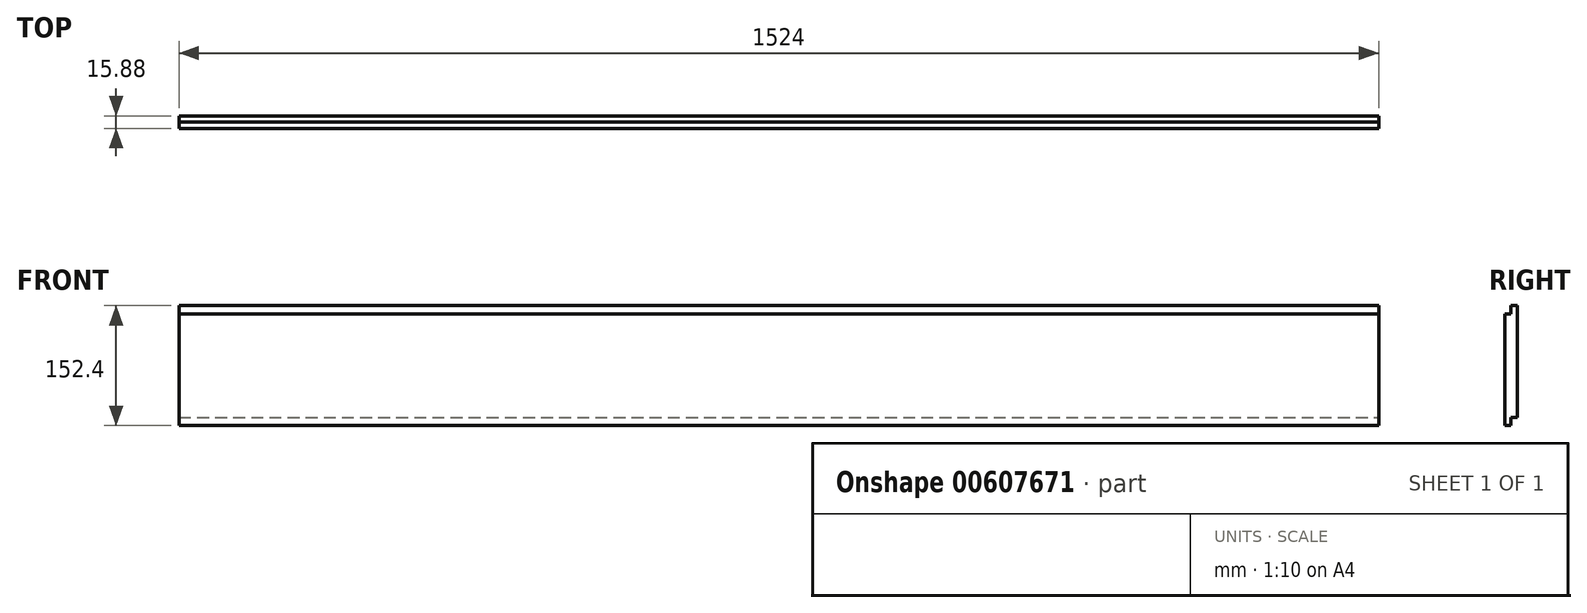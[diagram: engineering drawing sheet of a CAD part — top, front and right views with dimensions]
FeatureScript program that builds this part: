
annotation { "Feature Type Name" : "Feature", "Feature Type Description" : "" }
export const myFeature = defineFeature(function(context is Context, id is Id, definition is map)
    precondition{}
    {
        {
            var Q0;
            Q0=qCreatedBy(makeId("Front.planeOp"),FACE);
            var sketch = newSketch(context, id + "F0", { "sketchPlane" : qUnion([Q0])});
            skLineSegment(sketch, "E0", {"start": v(0, 0) * mm, "end": v(762, 0) * mm});
            skLineSegment(sketch, "E1", {"start": v(762, 0) * mm, "end": v(762, 76.2) * mm});
            skLineSegment(sketch, "E2.bottom", {"start": v(762, 76.2) * mm, "end": v(-762, 76.2) * mm});
            skLineSegment(sketch, "E2.top", {"start": v(762, -76.2) * mm, "end": v(-762, -76.2) * mm});
            skLineSegment(sketch, "E2.left", {"start": v(762, 76.2) * mm, "end": v(762, -76.2) * mm});
            skLineSegment(sketch, "E2.right", {"start": v(-762, 76.2) * mm, "end": v(-762, -76.2) * mm});
            skPoint(sketch, "E2.middle", {"position": v(0, 0) * mm});
            skSolve(sketch);
        }
        {
            var Q0;
            Q0 = qSketchRegion(id + "F0", true);
            extrude(context, id + "F1", {"entities" : qUnion([Q0]), "depth" : 15.88 * mm, "offsetDistance" : 25.4 * mm});
        }
        {
            var Q0;
            Q0=makeQuery(id+"F1.opExtrude","SWEPT_FACE",FACE,{"disambiguationData":[OSD([sQuery(id+"F0.wireOp",EDGE,"E2.left")])]});
            var sketch = newSketch(context, id + "F2", { "sketchPlane" : qUnion([Q0])});
            skLineSegment(sketch, "E3", {"start": v(0, 76.2) * mm, "end": v(-7.87, 76.2) * mm});
            skLineSegment(sketch, "E4", {"start": v(-7.87, 76.2) * mm, "end": v(-7.87, 65.79) * mm});
            skLineSegment(sketch, "E5.bottom", {"start": v(-15.88, 76.2) * mm, "end": v(-7.87, 76.2) * mm});
            skLineSegment(sketch, "E5.top", {"start": v(-15.88, 65.79) * mm, "end": v(-7.87, 65.79) * mm});
            skLineSegment(sketch, "E5.left", {"start": v(-15.88, 76.2) * mm, "end": v(-15.88, 65.79) * mm});
            skLineSegment(sketch, "E6", {"start": v(-15.88, -76.2) * mm, "end": v(-8, -76.2) * mm});
            skLineSegment(sketch, "E7", {"start": v(-8, -76.2) * mm, "end": v(-8, -65.79) * mm});
            skLineSegment(sketch, "E8.bottom", {"start": v(0, -76.2) * mm, "end": v(-8, -76.2) * mm});
            skLineSegment(sketch, "E8.top", {"start": v(0, -65.79) * mm, "end": v(-8, -65.79) * mm});
            skLineSegment(sketch, "E8.left", {"start": v(0, -76.2) * mm, "end": v(0, -65.79) * mm});
            skSolve(sketch);
        }
        {
            var Q0;
            Q0=makeQuery(id+"F2.imprint","IMPRINT",FACE,{"disambiguationData":[TD([[makeQuery(id+"F2.imprint","IMPRINT",EDGE,{"derivedFrom":sQuery(id+"F2.wireOp",EDGE,"E8.bottom")}),1.0]])]});
            var Q1;
            Q1=makeQuery(id+"F2.imprint","IMPRINT",FACE,{"disambiguationData":[TD([[makeQuery(id+"F2.imprint","IMPRINT",EDGE,{"derivedFrom":sQuery(id+"F2.wireOp",EDGE,"E5.bottom")}),-1.0]])]});
            extrude(context, id + "F3", {"entities" : qUnion([Q0, Q1]), "operationType" : NewBodyOperationType.REMOVE, "endBound" : BoundingType.UP_TO_NEXT, "oppositeDirection" : true, "depth" : 25.4 * mm, "offsetDistance" : 25.4 * mm});
        }
    });
